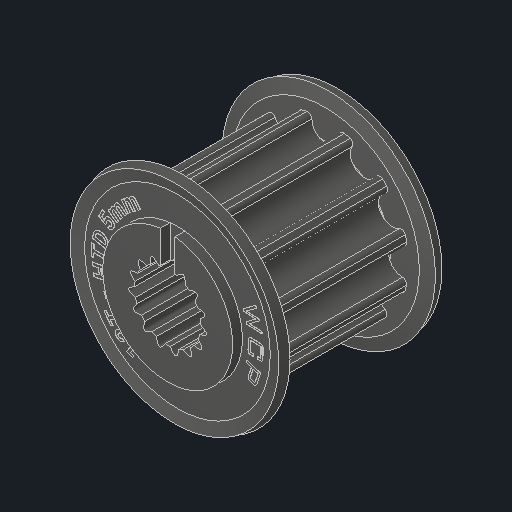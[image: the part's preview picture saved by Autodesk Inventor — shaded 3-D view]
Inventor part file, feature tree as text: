
AUTODESK INVENTOR PART (.ipt)
format: ipt  version: 2023.4 (Build 274418000, 418)  size: 565,760 bytes
history: native  units: in
note: dims shown in document units (in); Inventor stores cm internally (conversion verified against a paired STEP export)
features: other x2, mirror x1
ambient origin geometry x8: Origin, YZ Plane, XZ Plane, XY Plane, X Axis, Y Axis, Z Axis, Center Point
bodies: Solid1 (feature_tree), Solid2 (feature_tree), Solid3 (feature_tree)
feature tree (3):
  mirror  "Mirror2"
  other  "Cut-Extrude1"
  other  "Cut-Extrude2"
